# Revit family: РОСМА_МанометрОсевойЭлектроконтактнойПриставкой
name_source: partatom
category: Арматура трубопроводов
revit_build: Autodesk Revit 2018 (Build: 20180423_1000(x64)
units: mm (PartAtom-declared; Revit-internal decimal feet)

## family parameters
Всегда вертикально = Да
На основе рабочей плоскости = Нет
Общий = Нет
При загрузке вырезать с полостями = Нет
Размер круглого соединителя = Использовать диаметр
Тип детали = Вставляется

## types (1)
- 310
    ADSK_Единица измерения = шт.
    ADSK_Количество = 1
    D1 = 60 мм
    D2 = 59 мм
    D2/2 = 30 мм
    DN = 8.00 мм
    Ddempfer = 5 мм
    Dgol = 10 мм
    Drezba = 12 мм
    Dполости_переднСт = 53 мм
    Lgol = 2 мм
    R1 шкала = 21 мм
    R2 шкала = 20 мм
    R_Logo = 16 мм
    Rg1 = 6 мм
    Rg2 = 11 мм
    S = 10 мм
    Table = спец_осевой с электроконтактной приставкой
    URL = https://rosma.spb.ru
    b = 30 мм
    b-e = 13 мм
    b1 = 86 мм
    e = 17 мм
    f = 19 мм
    h_rezba = 15 мм
    h_гайки = 10 мм
    m = 30 мм
    Группа модели = Оборудование
    Давление01 = ‎ : ТВ -0.1…0МПа
    Давление03 = ‎ : ТМ 0…0.1МПа
    Давление04 = ‎ : ТМ 0…0.16МПа
    Давление05 = ‎ : ТМ 0…0.25МПа
    Давление06 = ‎ : ТМ 0…0.4МПа
    Давление07 = ‎ : ТМ 0…0.6МПа
    Давление08 = ‎ : ТМ 0…1.0МПа
    Давление09 = ‎ : ТМ 0…1.6МПа
    Давление10 = ‎ : ТМ 0…2.5МПа
    Давление11 = ‎ : ТМ 0…4МПа
    Давление12 = ‎ : ТМ 0…6МПа
    Давление13 = ‎ : ТМ 0…10МПа
    Давление14 = ‎ : ТМ 0…16МПа
    Давление15 = ‎ : ТМ 0…25МПа
    Давление19 = ‎ : ТМВ -0.1…0.15МПа
    Давление20 = ‎ : ТМВ -0.1…0.3МПа
    Давление21 = ‎ : ТМВ -0.1…0.5МПа
    Давление22 = ‎ : ТМВ -0.1…0.9МПа
    Давление23 = ‎ : ТМВ -0.1…1.5МПа
    Давление24 = ‎ : ТМВ -0.1…2.4МПа
    Диапазон раб. температур измер. среды = −50°C…+150°C
    Диапазон раб. температур окр. среды = −60°C…+60°C
    Длина стрелки = 20 мм
    Изготовитель = ЗАО "РОСМА"
    Исполнение = 310
    Класс точности = 2,5
    Климатическое исполнение = Группа В3 по ГОСТ Р 52931; климатическое исполнение УХЛ категории 3.1 по ГОСТ 15150
    Код IP = IP40
    Межпроверочный интервал = 2 года
    Описание = Манометр показывающий ТМ, серия 10. Манометры осевые с электроконтактной приставкой предназначены для управления внешними электрическими цепями в схемах сигнализации, автоматики и блокировки технологических процессов.
    Присоединение = Осевое
    Техническая документация = ТУ 4212-001-4719015564-2008; ГОСТ 2405–88
